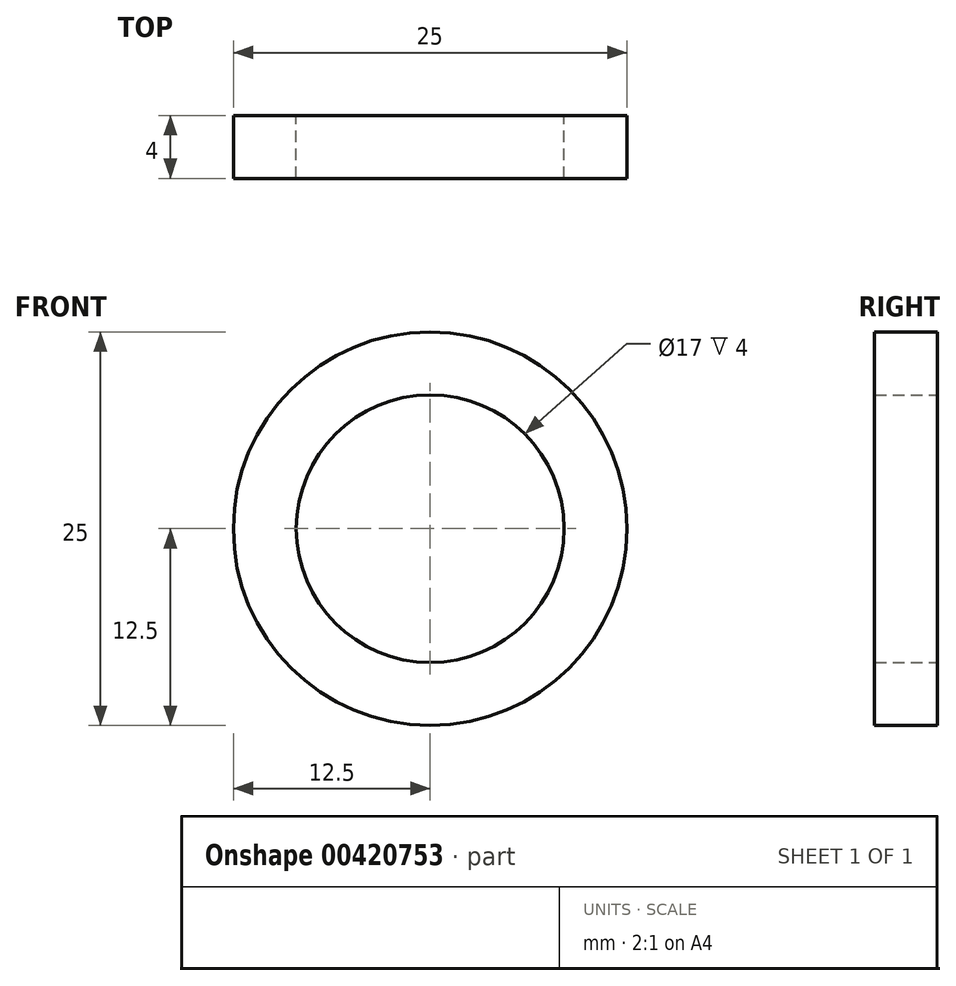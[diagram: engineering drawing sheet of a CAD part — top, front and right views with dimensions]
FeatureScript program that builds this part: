
annotation { "Feature Type Name" : "Feature", "Feature Type Description" : "" }
export const myFeature = defineFeature(function(context is Context, id is Id, definition is map)
    precondition{}
    {
        {
            var Q0;
            Q0=qCreatedBy(makeId("Front.planeOp"),FACE);
            var sketch = newSketch(context, id + "F0", { "sketchPlane" : qUnion([Q0])});
            skCircle(sketch, "E0", {"center": v(0, 0) * mm, "radius": 12.5 * mm});
            skCircle(sketch, "E1", {"center": v(0, 0) * mm, "radius": 8.5 * mm});
            skSolve(sketch);
        }
        {
            var Q0;
            Q0=makeQuery(id+"F0.imprint","IMPRINT",FACE,{"disambiguationData":[TD([[makeQuery(id+"F0.imprint","IMPRINT",EDGE,{"derivedFrom":sQuery(id+"F0.wireOp",EDGE,"E0")}),1.0]])]});
            extrude(context, id + "F1", {"entities" : qUnion([Q0]), "depth" : 4 * mm});
        }
    });
